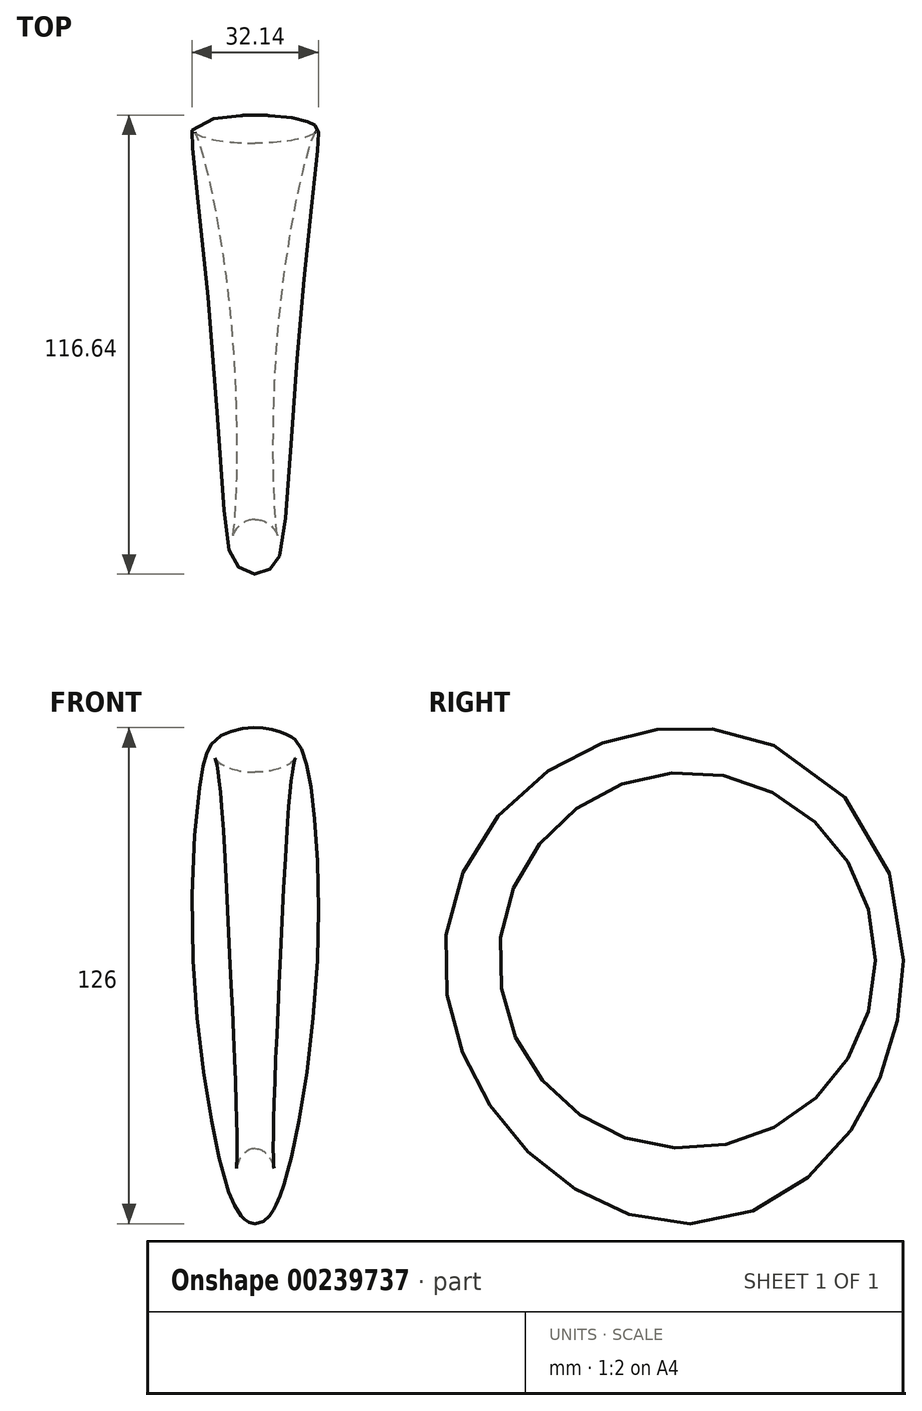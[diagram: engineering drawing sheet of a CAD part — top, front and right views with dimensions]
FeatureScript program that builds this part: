
annotation { "Feature Type Name" : "Feature", "Feature Type Description" : "" }
export const myFeature = defineFeature(function(context is Context, id is Id, definition is map)
    precondition{}
    {
        {
            var Q0;
            Q0=qCreatedBy(makeId("Right.planeOp"),FACE);
            var sketch = newSketch(context, id + "F0", { "sketchPlane" : qUnion([Q0])});
            skCircle(sketch, "E0", {"center": v(0, 0) * mm, "radius": 47.81 * mm});
            skSolve(sketch);
        }
        {
            var Q0;
            Q0=qCreatedBy(makeId("Front.planeOp"),FACE);
            var sketch = newSketch(context, id + "F1", { "sketchPlane" : qUnion([Q0])});
            skLineSegment(sketch, "E1.0", {"start": v(0, 47.81) * mm, "end": v(0, -47.81) * mm});
            skEllipse(sketch, "E2", {"center": v(0, 53.46) * mm, "majorRadius": 5.65 * mm, "minorRadius": 11.22 * mm, "majorAxis": v(0, -1)});
            skEllipse(sketch, "E3", {"center": v(0, -57.36) * mm, "majorRadius": 9.55 * mm, "minorRadius": 5.8 * mm, "majorAxis": v(0, 1)});
            skSolve(sketch);
        }
        {
            var Q0;
            Q0=qCreatedBy(makeId("Top.planeOp"),FACE);
            var sketch = newSketch(context, id + "F2", { "sketchPlane" : qUnion([Q0])});
            skLineSegment(sketch, "E4.0", {"start": v(0, 47.81) * mm, "end": v(0, -47.81) * mm});
            skEllipse(sketch, "E5", {"center": v(0, -54.77) * mm, "majorRadius": 6.96 * mm, "minorRadius": 6.4 * mm, "majorAxis": v(0, 1)});
            skEllipse(sketch, "E6", {"center": v(0, 51.36) * mm, "majorRadius": 3.55 * mm, "minorRadius": 15.79 * mm, "majorAxis": v(0, -1)});
            skSolve(sketch);
        }
        {
            var Q0;
            Q0=makeQuery(id+"F2.imprint","IMPRINT",FACE,{"disambiguationData":[TD([[makeQuery(id+"F2.imprint","IMPRINT",EDGE,{"derivedFrom":sQuery(id+"F2.wireOp",EDGE,"E6")}),1.0]])]});
            var Q1;
            Q1=makeQuery(id+"F1.imprint","IMPRINT",FACE,{"disambiguationData":[TD([[makeQuery(id+"F1.imprint","IMPRINT",EDGE,{"derivedFrom":sQuery(id+"F1.wireOp",EDGE,"E3")}),1.0]])]});
            var Q2;
            Q2=makeQuery(id+"F2.imprint","IMPRINT",FACE,{"disambiguationData":[TD([[makeQuery(id+"F2.imprint","IMPRINT",EDGE,{"derivedFrom":sQuery(id+"F2.wireOp",EDGE,"E5")}),1.0]])]});
            var Q3;
            Q3=makeQuery(id+"F1.imprint","IMPRINT",FACE,{"disambiguationData":[TD([[makeQuery(id+"F1.imprint","IMPRINT",EDGE,{"derivedFrom":sQuery(id+"F1.wireOp",EDGE,"E2")}),1.0]])]});
            var Q4;
            Q4=sQuery(id+"F0.wireOp",EDGE,"E0");
            loft(context, id + "F3", {"addGuides" : true, "sheetProfilesArray" : [{ "sheetProfileEntities" : qUnion([Q0]) }, { "sheetProfileEntities" : qUnion([Q1]) }, { "sheetProfileEntities" : qUnion([Q2]) }, { "sheetProfileEntities" : qUnion([Q3]) }], "guidesArray" : [{ "guideEntities" : qUnion([Q4]), "guideDerivativeType" : LoftGuideDerivativeType.DEFAULT, "guideDerivativeMagnitude" : 1 }]});
        }
    });
